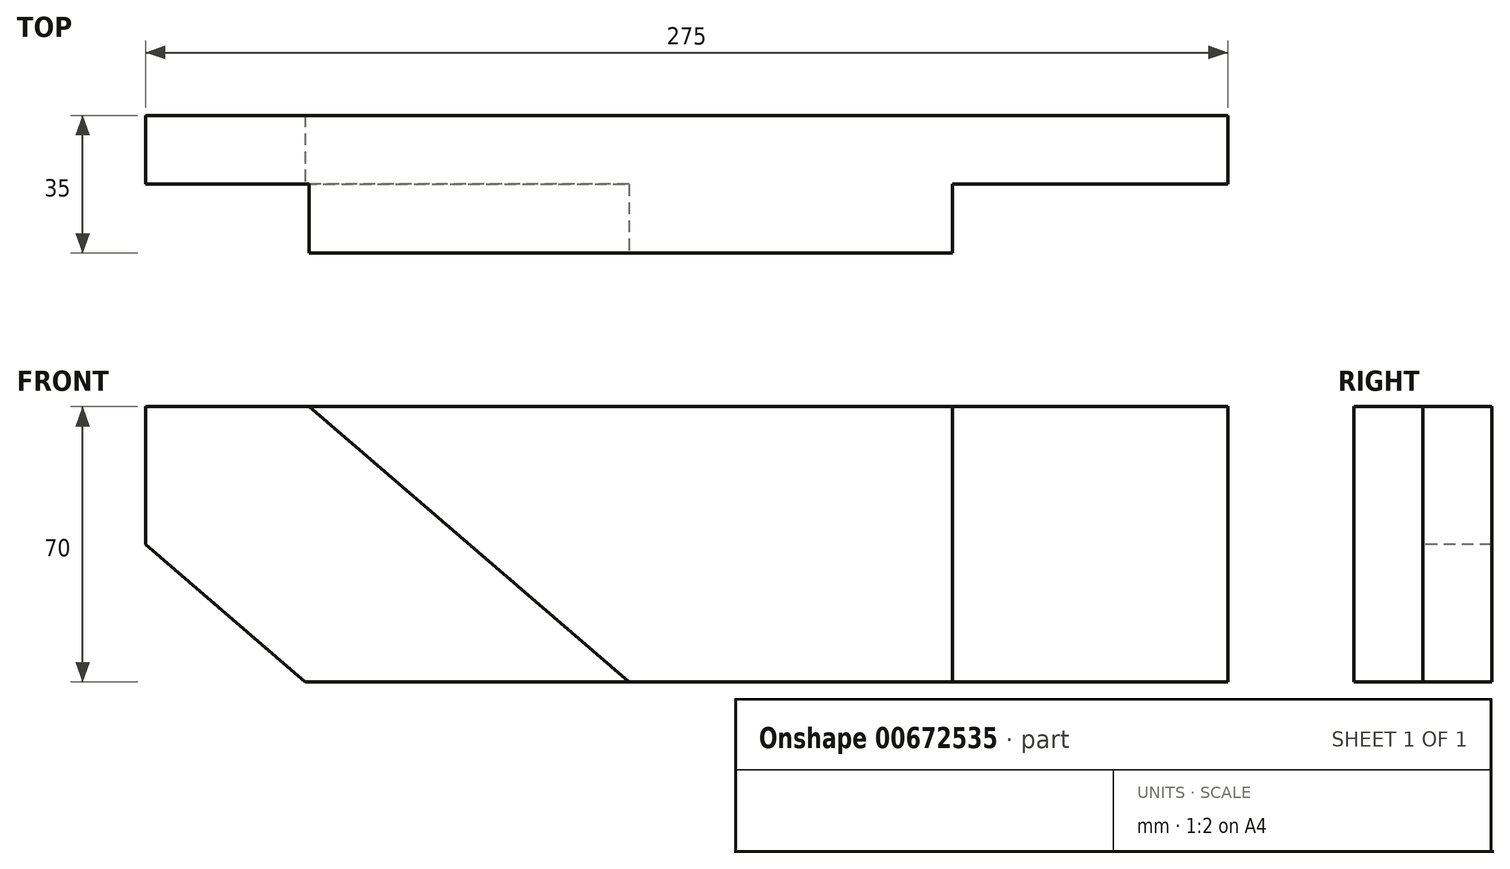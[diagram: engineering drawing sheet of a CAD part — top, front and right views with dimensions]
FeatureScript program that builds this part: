
annotation { "Feature Type Name" : "Feature", "Feature Type Description" : "" }
export const myFeature = defineFeature(function(context is Context, id is Id, definition is map)
    precondition{}
    {
        {
            var Q0;
            Q0=qCreatedBy(makeId("Front.planeOp"),FACE);
            var sketch = newSketch(context, id + "F0", { "sketchPlane" : qUnion([Q0])});
            skLineSegment(sketch, "E0.bottom", {"start": v(0, 0) * mm, "end": v(275, 0) * mm});
            skLineSegment(sketch, "E0.top", {"start": v(0, 70) * mm, "end": v(275, 70) * mm});
            skLineSegment(sketch, "E0.left", {"start": v(0, 0) * mm, "end": v(0, 70) * mm});
            skLineSegment(sketch, "E0.right", {"start": v(275, 0) * mm, "end": v(275, 70) * mm});
            skSolve(sketch);
        }
        {
            var Q0;
            Q0=makeQuery(id+"F0.imprint","IMPRINT",FACE,{"disambiguationData":[TD([[makeQuery(id+"F0.imprint","IMPRINT",EDGE,{"derivedFrom":sQuery(id+"F0.wireOp",EDGE,"E0.bottom")}),1.0]])]});
            extrude(context, id + "F1", {"entities" : qUnion([Q0]), "depth" : 35 * mm, "offsetDistance" : 25 * mm});
        }
        {
            var Q0;
            Q0=makeQuery(id+"F1.opExtrude","SWEPT_FACE",FACE,{"disambiguationData":[OSD([sQuery(id+"F0.wireOp",EDGE,"E0.bottom")])]});
            var sketch = newSketch(context, id + "F2", { "sketchPlane" : qUnion([Q0])});
            skLineSegment(sketch, "E1", {"start": v(205, 35) * mm, "end": v(205, 17.5) * mm});
            skLineSegment(sketch, "E2", {"start": v(205, 17.5) * mm, "end": v(275, 17.5) * mm});
            skSolve(sketch);
        }
        {
            var Q0;
            {var subQ0=sQuery(id+"F2.wireOp",EDGE,"E1");Q0=makeQuery(id+"F2.imprint","IMPRINT",FACE,{"disambiguationData":[TD([[makeQuery(id+"F2.imprint","IMPRINT",EDGE,{"derivedFrom":subQ0}),1.0]])]});}
            extrude(context, id + "F3", {"entities" : qUnion([Q0]), "operationType" : NewBodyOperationType.REMOVE, "endBound" : BoundingType.THROUGH_ALL, "oppositeDirection" : true, "depth" : 25 * mm, "offsetDistance" : 25 * mm});
        }
        {
            var Q0;
            Q0=makeQuery(id+"F1.opExtrude","CAP_FACE",FACE,{"disambiguationData":[OSD([sQuery(id+"F0.wireOp",EDGE,"E0.bottom"),sQuery(id+"F0.wireOp",EDGE,"E0.top"),sQuery(id+"F0.wireOp",EDGE,"E0.left"),sQuery(id+"F0.wireOp",EDGE,"E0.right")])],"isStart":false});
            var sketch = newSketch(context, id + "F4", { "sketchPlane" : qUnion([Q0])});
            skLineSegment(sketch, "E3", {"start": v(0, 35) * mm, "end": v(40.59, 0) * mm});
            skSolve(sketch);
        }
        {
            var Q0;
            {var subQ0=sQuery(id+"F4.wireOp",EDGE,"E3");Q0=makeQuery(id+"F4.imprint","IMPRINT",FACE,{"disambiguationData":[TD([[makeQuery(id+"F4.imprint","IMPRINT",EDGE,{"derivedFrom":subQ0}),-1.0]])]});}
            extrude(context, id + "F5", {"entities" : qUnion([Q0]), "operationType" : NewBodyOperationType.REMOVE, "endBound" : BoundingType.THROUGH_ALL, "oppositeDirection" : true, "depth" : 25 * mm, "offsetDistance" : 25 * mm});
        }
        {
            var Q0;
            Q0=makeQuery(id+"F1.opExtrude","CAP_FACE",FACE,{"disambiguationData":[OSD([sQuery(id+"F0.wireOp",EDGE,"E0.bottom"),sQuery(id+"F0.wireOp",EDGE,"E0.top"),sQuery(id+"F0.wireOp",EDGE,"E0.left"),sQuery(id+"F0.wireOp",EDGE,"E0.right")])],"isStart":false});
            var sketch = newSketch(context, id + "F6", { "sketchPlane" : qUnion([Q0])});
            skLineSegment(sketch, "E4", {"start": v(122.8, 0) * mm, "end": v(41.62, 70) * mm});
            skSolve(sketch);
        }
        {
            var Q0;
            {var subQ2=sQuery(id+"F6.wireOp",EDGE,"E4");Q0=makeQuery(id+"F6.imprint","IMPRINT",FACE,{"disambiguationData":[TD([[makeQuery(id+"F6.imprint","IMPRINT",EDGE,{"derivedFrom":subQ2}),1.0]])]});}
            extrude(context, id + "F7", {"entities" : qUnion([Q0]), "operationType" : NewBodyOperationType.REMOVE, "oppositeDirection" : true, "depth" : 17.5 * mm, "offsetDistance" : 25 * mm});
        }
    });
